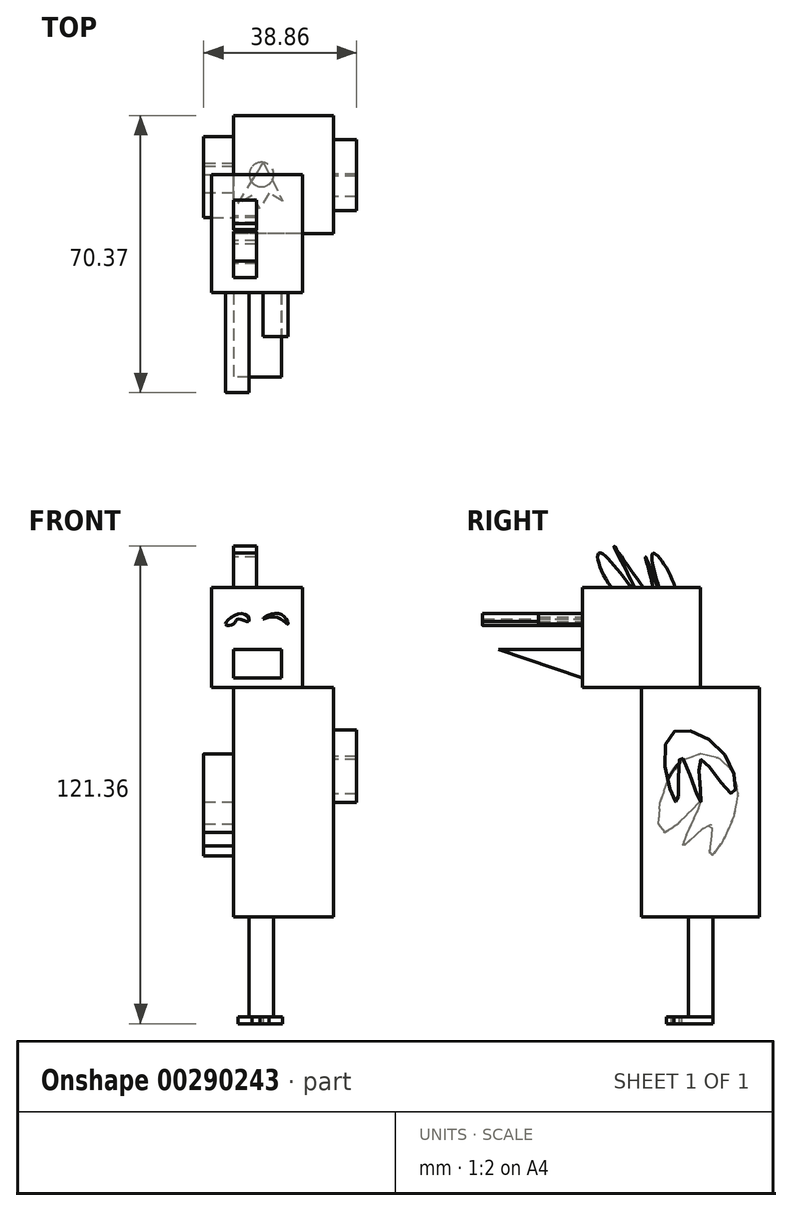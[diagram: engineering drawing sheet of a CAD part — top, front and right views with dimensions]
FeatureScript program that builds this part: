
annotation { "Feature Type Name" : "Feature", "Feature Type Description" : "" }
export const myFeature = defineFeature(function(context is Context, id is Id, definition is map)
    precondition{}
    {
        {
            var Q0;
            Q0=qCreatedBy(makeId("Right.planeOp"),FACE);
            var sketch = newSketch(context, id + "F0", { "sketchPlane" : qUnion([Q0])});
            skLineSegment(sketch, "E0.bottom", {"start": v(-14.99, 29.14) * mm, "end": v(14.99, 29.14) * mm});
            skLineSegment(sketch, "E0.top", {"start": v(-14.99, -29.14) * mm, "end": v(14.99, -29.14) * mm});
            skLineSegment(sketch, "E0.left", {"start": v(-14.99, 29.14) * mm, "end": v(-14.99, -29.14) * mm});
            skLineSegment(sketch, "E0.right", {"start": v(14.99, 29.14) * mm, "end": v(14.99, -29.14) * mm});
            skPoint(sketch, "E0.middle", {"position": v(0, 0) * mm});
            skSolve(sketch);
        }
        {
            var Q0;
            Q0=makeQuery(id+"F0.imprint","IMPRINT",FACE,{"disambiguationData":[TD([[makeQuery(id+"F0.imprint","IMPRINT",EDGE,{"derivedFrom":sQuery(id+"F0.wireOp",EDGE,"E0.bottom")}),-1.0]])]});
            extrude(context, id + "F1", {"entities" : qUnion([Q0]), "depth" : 25.4 * mm});
        }
        {
            var Q0;
            Q0=makeQuery(id+"F1.opExtrude","SWEPT_FACE",FACE,{"disambiguationData":[OSD([sQuery(id+"F0.wireOp",EDGE,"E0.top")])]});
            var sketch = newSketch(context, id + "F2", { "sketchPlane" : qUnion([Q0])});
            skCircle(sketch, "E1", {"center": v(18.61, 0) * mm, "radius": 2.54 * mm});
            skCircle(sketch, "E2", {"center": v(7.05, 0) * mm, "radius": 3.11 * mm});
            skSolve(sketch);
        }
        {
            var Q0;
            Q0=makeQuery(id+"F2.imprint","IMPRINT",FACE,{"disambiguationData":[TD([[makeQuery(id+"F2.imprint","IMPRINT",EDGE,{"derivedFrom":sQuery(id+"F2.wireOp",EDGE,"E2")}),1.0]])]});
            extrude(context, id + "F3", {"entities" : qUnion([Q0]), "operationType" : NewBodyOperationType.ADD, "depth" : 25.4 * mm});
        }
        {
            var Q0;
            Q0=makeQuery(id+"F3.opExtrude","CAP_FACE",FACE,{"disambiguationData":[OSD([sQuery(id+"F2.wireOp",EDGE,"E2")])],"isStart":false});
            var sketch = newSketch(context, id + "F4", { "sketchPlane" : qUnion([Q0])});
            skLineSegment(sketch, "E3", {"start": v(7.55, -3.07) * mm, "end": v(12.44, 6.75) * mm});
            skLineSegment(sketch, "E4", {"start": v(12.44, 6.75) * mm, "end": v(8.95, 4.71) * mm});
            skLineSegment(sketch, "E5", {"start": v(8.95, 4.71) * mm, "end": v(6.63, 8.7) * mm});
            skLineSegment(sketch, "E6", {"start": v(6.63, 8.7) * mm, "end": v(4.64, 5.33) * mm});
            skLineSegment(sketch, "E7", {"start": v(4.64, 5.33) * mm, "end": v(1.1, 7.41) * mm});
            skLineSegment(sketch, "E8", {"start": v(1.1, 7.41) * mm, "end": v(7.55, -3.07) * mm});
            skSolve(sketch);
        }
        {
            var Q0;
            {var subQ1=sQuery(id+"F4.wireOp",EDGE,"E3");var subQ2=makeQuery(id+"F3.opExtrude","CAP_EDGE",EDGE,{"disambiguationData":[OSD([sQuery(id+"F2.wireOp",EDGE,"E2")])],"isStart":false});var subQ4=makeQuery(id+"F4.imprint","INTERSECT",VERTEX,{"derivedFrom":[subQ2,subQ1]});Q0=makeQuery(id+"F4.imprint","IMPRINT",FACE,{"disambiguationData":[TD([[makeQuery(id+"F4.imprint","IMPRINT",EDGE,{"disambiguationData":[TD([[subQ4,-1.0]])],"derivedFrom":subQ2}),1.0]])]});}
            var Q1;
            {var subQ0=sQuery(id+"F4.wireOp",EDGE,"E4");Q1=makeQuery(id+"F4.imprint","IMPRINT",FACE,{"disambiguationData":[TD([[makeQuery(id+"F4.imprint","IMPRINT",EDGE,{"derivedFrom":subQ0}),1.0]])]});}
            extrude(context, id + "F5", {"entities" : qUnion([Q0, Q1]), "operationType" : NewBodyOperationType.ADD, "depth" : 1.78 * mm});
        }
        {
            var Q0;
            Q0=makeQuery(id+"F1.opExtrude","CAP_FACE",FACE,{"disambiguationData":[OSD([sQuery(id+"F0.wireOp",EDGE,"E0.bottom"),sQuery(id+"F0.wireOp",EDGE,"E0.top"),sQuery(id+"F0.wireOp",EDGE,"E0.left"),sQuery(id+"F0.wireOp",EDGE,"E0.right")])],"isStart":true});
            var sketch = newSketch(context, id + "F6", { "sketchPlane" : qUnion([Q0])});
            skFitSpline(sketch, "E9", {"points": [v(4.71, 10.5) * mm, v(9.33, -7.68) * mm, v(0, 0) * mm, v(4.56, -11.2) * mm, v(-2.51, -5.61) * mm, v(-2.24, -13.6) * mm, v(-9.52, 4.22) * mm, v(4.71, 10.5) * mm]});
            skSolve(sketch);
        }
        {
            var Q0;
            Q0=makeQuery(id+"F6.imprint","IMPRINT",FACE,{"disambiguationData":[TD([[makeQuery(id+"F6.imprint","IMPRINT",EDGE,{"derivedFrom":sQuery(id+"F6.wireOp",EDGE,"E9")}),-1.0]])]});
            extrude(context, id + "F7", {"entities" : qUnion([Q0]), "operationType" : NewBodyOperationType.ADD, "depth" : 7.62 * mm});
        }
        {
            var Q0;
            Q0=makeQuery(id+"F1.opExtrude","CAP_FACE",FACE,{"disambiguationData":[OSD([sQuery(id+"F0.wireOp",EDGE,"E0.bottom"),sQuery(id+"F0.wireOp",EDGE,"E0.top"),sQuery(id+"F0.wireOp",EDGE,"E0.left"),sQuery(id+"F0.wireOp",EDGE,"E0.right")])],"isStart":false});
            var sketch = newSketch(context, id + "F8", { "sketchPlane" : qUnion([Q0])});
            skFitSpline(sketch, "E10", {"points": [v(11.16, 26.4) * mm, v(15.78, 8.2) * mm, v(6.45, 15.89) * mm, v(11.01, 4.7) * mm, v(3.94, 10.27) * mm, v(4.21, 2.28) * mm, v(-3.07, 20.11) * mm, v(11.16, 26.4) * mm]});
            skSolve(sketch);
        }
        {
            var Q0;
            Q0=sQuery(id+"F8.wireOp",EDGE,"E10");
            extrude(context, id + "F9", {"bodyType" : ToolBodyType.SURFACE, "surfaceEntities" : qUnion([Q0]), "depth" : 7.11 * mm});
        }
        {
            var Q0;
            Q0=makeQuery(id+"F1.opExtrude","SWEPT_FACE",FACE,{"disambiguationData":[OSD([sQuery(id+"F0.wireOp",EDGE,"E0.bottom")])]});
            var sketch = newSketch(context, id + "F10", { "sketchPlane" : qUnion([Q0])});
            skLineSegment(sketch, "E11.bottom", {"start": v(17.52, 0) * mm, "end": v(-5.6, 0) * mm});
            skLineSegment(sketch, "E11.top", {"start": v(17.52, -29.98) * mm, "end": v(-5.6, -29.98) * mm});
            skLineSegment(sketch, "E11.left", {"start": v(17.52, 0) * mm, "end": v(17.52, -29.98) * mm});
            skLineSegment(sketch, "E11.right", {"start": v(-5.6, 0) * mm, "end": v(-5.6, -29.98) * mm});
            skPoint(sketch, "E11.middle", {"position": v(5.96, -14.99) * mm});
            skSolve(sketch);
        }
        {
            var Q0;
            {var subQ2=sQuery(id+"F10.wireOp",EDGE,"E11.top");Q0=makeQuery(id+"F10.imprint","IMPRINT",FACE,{"disambiguationData":[TD([[makeQuery(id+"F10.imprint","IMPRINT",EDGE,{"derivedFrom":subQ2}),-1.0]])]});}
            var Q1;
            {var subQ0=sQuery(id+"F10.wireOp",EDGE,"E11.left");var subQ1=sQuery(id+"F10.wireOp",EDGE,"E11.bottom");var subQ2=makeQuery(id+"F10.imprint","INTERSECT",VERTEX,{"derivedFrom":[subQ1,subQ0]});Q1=makeQuery(id+"F10.imprint","IMPRINT",FACE,{"disambiguationData":[TD([[makeQuery(id+"F10.imprint","IMPRINT",EDGE,{"disambiguationData":[TD([[subQ2,-1.0]])],"derivedFrom":subQ1}),1.0]])]});}
            extrude(context, id + "F11", {"entities" : qUnion([Q0, Q1]), "operationType" : NewBodyOperationType.ADD, "depth" : 25.4 * mm});
        }
        {
            var Q0;
            Q0=qCreatedBy(makeId("Right.planeOp"),FACE);
            var sketch = newSketch(context, id + "F12", { "sketchPlane" : qUnion([Q0])});
            skLineSegment(sketch, "E12", {"start": v(-20.43, 38.7) * mm, "end": v(-51.43, 38.7) * mm});
            skLineSegment(sketch, "E13", {"start": v(-51.43, 38.7) * mm, "end": v(-22.87, 29.16) * mm});
            skLineSegment(sketch, "E14", {"start": v(-22.87, 29.16) * mm, "end": v(-20.43, 38.7) * mm});
            skSolve(sketch);
        }
        {
            var Q0;
            Q0=makeQuery(id+"F12.imprint","IMPRINT",FACE,{"disambiguationData":[TD([[makeQuery(id+"F12.imprint","IMPRINT",EDGE,{"derivedFrom":sQuery(id+"F12.wireOp",EDGE,"E12")}),1.0]])]});
            extrude(context, id + "F13", {"entities" : qUnion([Q0]), "operationType" : NewBodyOperationType.ADD, "depth" : 12.2 * mm});
        }
        {
            var Q0;
            Q0=makeQuery(id+"F11.opExtrude","SWEPT_FACE",FACE,{"disambiguationData":[OSD([sQuery(id+"F10.wireOp",EDGE,"E11.top")])]});
            var sketch = newSketch(context, id + "F14", { "sketchPlane" : qUnion([Q0])});
            skFitSpline(sketch, "E15", {"points": [v(7.4, 46.53) * mm, v(11.53, 47.86) * mm, v(13.76, 45.2) * mm, v(10.75, 46.94) * mm, v(7.4, 46.53) * mm]});
            skSolve(sketch);
        }
        {
            var Q0;
            Q0=makeQuery(id+"F14.imprint","IMPRINT",FACE,{"disambiguationData":[TD([[makeQuery(id+"F14.imprint","IMPRINT",EDGE,{"derivedFrom":sQuery(id+"F14.wireOp",EDGE,"E15")}),-1.0]])]});
            extrude(context, id + "F15", {"entities" : qUnion([Q0]), "operationType" : NewBodyOperationType.ADD, "depth" : 11.18 * mm});
        }
        {
            var Q0;
            Q0=makeQuery(id+"F11.opExtrude","SWEPT_FACE",FACE,{"disambiguationData":[OSD([sQuery(id+"F10.wireOp",EDGE,"E11.top")])]});
            var sketch = newSketch(context, id + "F16", { "sketchPlane" : qUnion([Q0])});
            skFitSpline(sketch, "E16", {"points": [v(-2.07, 45.18) * mm, v(2.3, 47.88) * mm, v(3.82, 45.91) * mm, v(0.98, 46.48) * mm, v(0, 45.22) * mm, v(-2.07, 45.18) * mm]});
            skSolve(sketch);
        }
        {
            var Q0;
            Q0=makeQuery(id+"F16.imprint","IMPRINT",FACE,{"disambiguationData":[TD([[makeQuery(id+"F16.imprint","IMPRINT",EDGE,{"derivedFrom":sQuery(id+"F16.wireOp",EDGE,"E16")}),-1.0]])]});
            extrude(context, id + "F17", {"entities" : qUnion([Q0]), "operationType" : NewBodyOperationType.ADD, "depth" : 25.4 * mm});
        }
        {
            var Q0;
            Q0=qCreatedBy(makeId("Right.planeOp"),FACE);
            var sketch = newSketch(context, id + "F18", { "sketchPlane" : qUnion([Q0])});
            skFitSpline(sketch, "E17", {"points": [v(-6.34, 51.62) * mm, v(-12.29, 63.08) * mm, v(-9.79, 51.8) * mm, v(-14.02, 62.28) * mm, v(-12.36, 52.8) * mm, v(-22.03, 65.04) * mm, v(-16.38, 53.3) * mm, v(-25.37, 63.28) * mm, v(-21.17, 53.06) * mm, v(-6.34, 51.62) * mm]});
            skSolve(sketch);
        }
        {
            var Q0;
            Q0=makeQuery(id+"F18.imprint","IMPRINT",FACE,{"disambiguationData":[TD([[makeQuery(id+"F18.imprint","IMPRINT",EDGE,{"derivedFrom":sQuery(id+"F18.wireOp",EDGE,"E17")}),1.0]])]});
            extrude(context, id + "F19", {"entities" : qUnion([Q0]), "operationType" : NewBodyOperationType.ADD, "depth" : 5.84 * mm});
        }
        {
            var Q0;
            Q0=makeQuery(id+"F9.opExtrude","SWEPT_BODY",BODY,{"disambiguationData":[OSD([sQuery(id+"F8.wireOp",EDGE,"E10")])]});
            deleteBodies(context, id + "F20", {"entities" : qUnion([Q0])});
        }
        {
            var Q0;
            Q0=makeQuery(id+"F1.opExtrude","CAP_FACE",FACE,{"disambiguationData":[OSD([sQuery(id+"F0.wireOp",EDGE,"E0.bottom"),sQuery(id+"F0.wireOp",EDGE,"E0.top"),sQuery(id+"F0.wireOp",EDGE,"E0.left"),sQuery(id+"F0.wireOp",EDGE,"E0.right")])],"isStart":false});
            var sketch = newSketch(context, id + "F21", { "sketchPlane" : qUnion([Q0])});
            skFitSpline(sketch, "E18", {"points": [v(6.13, 11.9) * mm, v(7.8, 2.13) * mm, v(0, 10.71) * mm, v(0, 0) * mm, v(-5.06, 11.58) * mm, v(-6.04, 0) * mm, v(-8.36, 16.27) * mm, v(6.13, 11.9) * mm]});
            skSolve(sketch);
        }
        {
            var Q0;
            Q0 = qSketchRegion(id + "F21", true);
            extrude(context, id + "F22", {"entities" : qUnion([Q0]), "operationType" : NewBodyOperationType.ADD, "depth" : 5.84 * mm});
        }
    });
